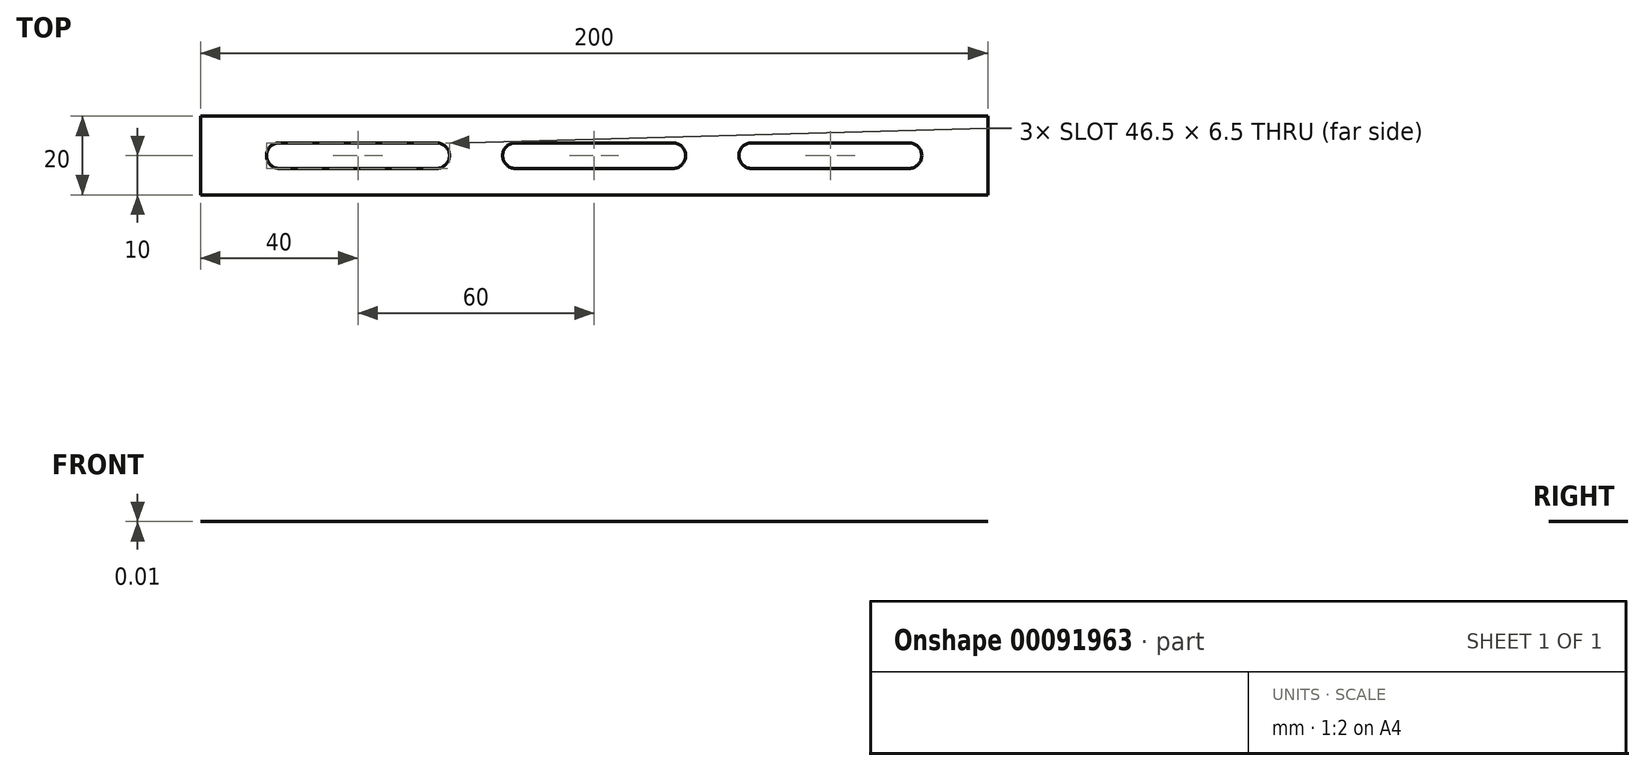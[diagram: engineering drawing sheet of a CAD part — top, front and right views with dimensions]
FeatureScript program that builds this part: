
annotation { "Feature Type Name" : "Feature", "Feature Type Description" : "" }
export const myFeature = defineFeature(function(context is Context, id is Id, definition is map)
    precondition{}
    {
        {
            var Q0;
            Q0=qCreatedBy(makeId("Top.planeOp"),FACE);
            var sketch = newSketch(context, id + "F0", { "sketchPlane" : qUnion([Q0])});
            skLineSegment(sketch, "E0.bottom", {"start": v(100, -10) * mm, "end": v(-100, -10) * mm});
            skLineSegment(sketch, "E0.top", {"start": v(100, 10) * mm, "end": v(-100, 10) * mm});
            skLineSegment(sketch, "E0.left", {"start": v(100, -10) * mm, "end": v(100, 10) * mm});
            skLineSegment(sketch, "E0.right", {"start": v(-100, -10) * mm, "end": v(-100, 10) * mm});
            skPoint(sketch, "E0.middle", {"position": v(0, 0) * mm});
            skLineSegment(sketch, "E1", {"start": v(0, 0) * mm, "end": v(-40, 0) * mm, "construction": true});
            skLineSegment(sketch, "E2", {"start": v(0, 0) * mm, "end": v(20, 0) * mm, "construction": true});
            skLineSegment(sketch, "E3", {"start": v(20, 0) * mm, "end": v(-20, 0) * mm});
            skArc(sketch, "E4.0.startCap", {"start": v(20, 3.25) * mm, "mid": v(23.25, 0) * mm, "end": v(20, -3.25) * mm});
            skArc(sketch, "E4.0.endCap", {"start": v(-20, -3.25) * mm, "mid": v(-23.25, 0) * mm, "end": v(-20, 3.25) * mm});
            skLineSegment(sketch, "E4.0.left", {"start": v(20, -3.25) * mm, "end": v(-20, -3.25) * mm});
            skLineSegment(sketch, "E4.0.right", {"start": v(20, 3.25) * mm, "end": v(-20, 3.25) * mm});
            skLineSegment(sketch, "E5", {"start": v(-40, 0) * mm, "end": v(-80, 0) * mm});
            skArc(sketch, "E6.0.startCap", {"start": v(-40, 3.25) * mm, "mid": v(-36.75, 0) * mm, "end": v(-40, -3.25) * mm});
            skArc(sketch, "E6.0.endCap", {"start": v(-80, -3.25) * mm, "mid": v(-83.25, 0) * mm, "end": v(-80, 3.25) * mm});
            skLineSegment(sketch, "E6.0.left", {"start": v(-40, -3.25) * mm, "end": v(-80, -3.25) * mm});
            skLineSegment(sketch, "E6.0.right", {"start": v(-40, 3.25) * mm, "end": v(-80, 3.25) * mm});
            skLineSegment(sketch, "E7.MirrorCS", {"start": v(40, -3.25) * mm, "end": v(80, -3.25) * mm});
            skArc(sketch, "E8.MirrorCS", {"start": v(40, 3.25) * mm, "mid": v(36.75, 0) * mm, "end": v(40, -3.25) * mm});
            skLineSegment(sketch, "E9.MirrorCS", {"start": v(40, 3.25) * mm, "end": v(80, 3.25) * mm});
            skArc(sketch, "E10.MirrorCS", {"start": v(80, -3.25) * mm, "mid": v(83.25, 0) * mm, "end": v(80, 3.25) * mm});
            skSolve(sketch);
        }
        {
            var Q0;
            Q0=makeQuery(id+"F0.imprint","IMPRINT",FACE,{"disambiguationData":[TD([[makeQuery(id+"F0.imprint","IMPRINT",EDGE,{"derivedFrom":sQuery(id+"F0.wireOp",EDGE,"E0.bottom")}),-1.0]])]});
            extrude(context, id + "F1", {"entities" : qUnion([Q0]), "depth" : 1 / 101.6 * mm});
        }
    });
